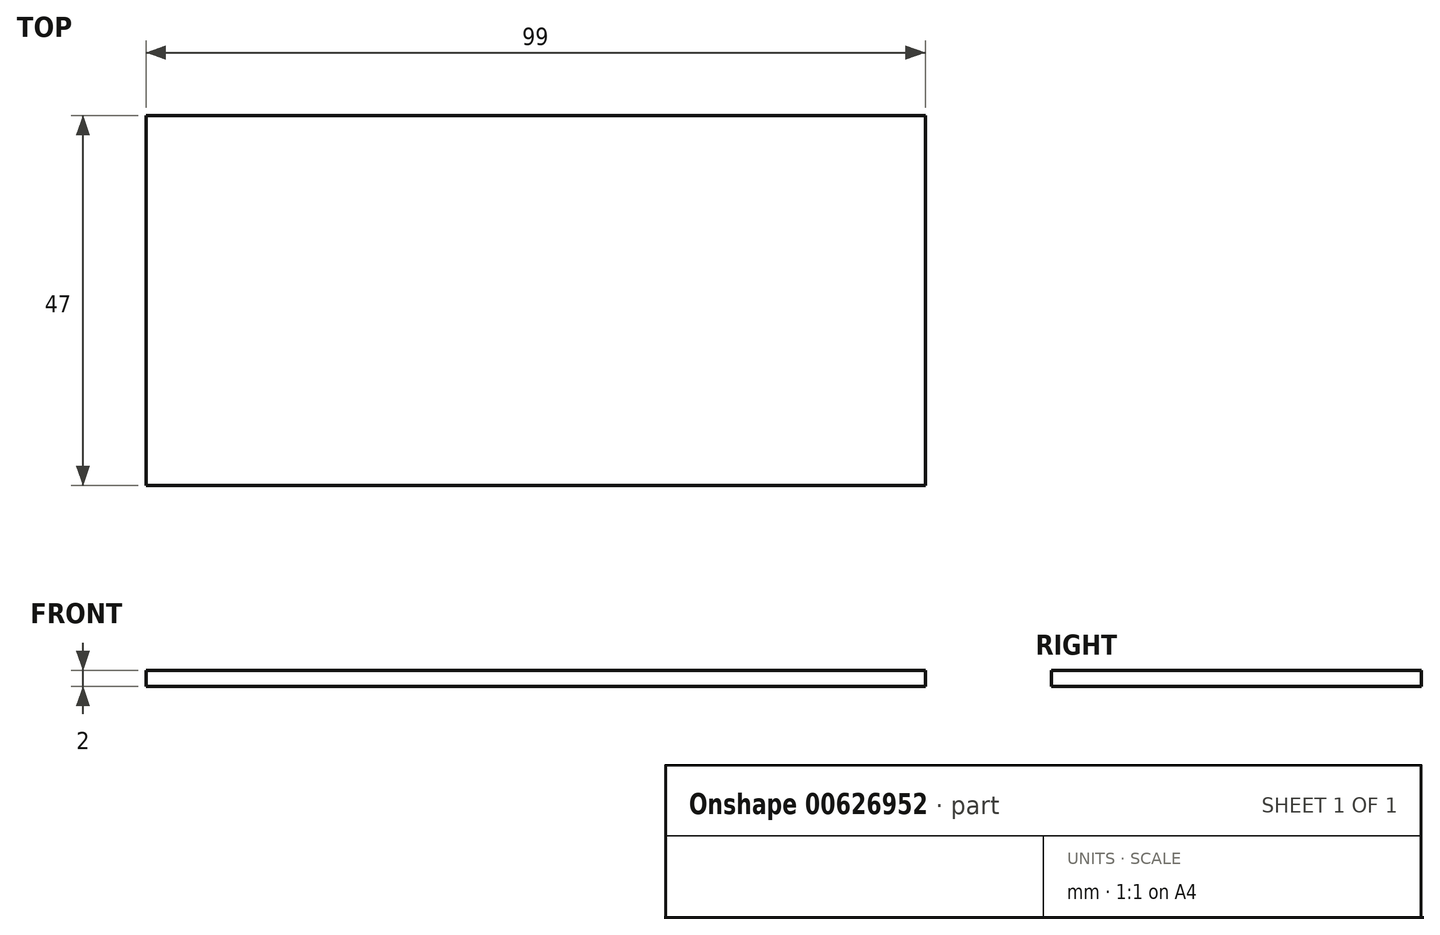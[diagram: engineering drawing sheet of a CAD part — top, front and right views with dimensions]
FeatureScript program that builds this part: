
annotation { "Feature Type Name" : "Feature", "Feature Type Description" : "" }
export const myFeature = defineFeature(function(context is Context, id is Id, definition is map)
    precondition{}
    {
        {
            var Q0;
            Q0=qCreatedBy(makeId("Top.planeOp"),FACE);
            var sketch = newSketch(context, id + "F0", { "sketchPlane" : qUnion([Q0])});
            skLineSegment(sketch, "E0.bottom", {"start": v(49.5, 23.5) * mm, "end": v(-49.5, 23.5) * mm});
            skLineSegment(sketch, "E0.top", {"start": v(49.5, -23.5) * mm, "end": v(-49.5, -23.5) * mm});
            skLineSegment(sketch, "E0.left", {"start": v(49.5, 23.5) * mm, "end": v(49.5, -23.5) * mm});
            skLineSegment(sketch, "E0.right", {"start": v(-49.5, 23.5) * mm, "end": v(-49.5, -23.5) * mm});
            skPoint(sketch, "E0.middle", {"position": v(0, 0) * mm});
            skLineSegment(sketch, "E1", {"start": v(28.5, -23.5) * mm, "end": v(28.5, 3.46) * mm, "construction": true});
            skSolve(sketch);
        }
        {
            var Q0;
            Q0=makeQuery(id+"F0.imprint","IMPRINT",FACE,{"disambiguationData":[TD([[makeQuery(id+"F0.imprint","IMPRINT",EDGE,{"derivedFrom":sQuery(id+"F0.wireOp",EDGE,"E0.bottom")}),1.0]])]});
            extrude(context, id + "F1", {"entities" : qUnion([Q0]), "depth" : 2 * mm, "offsetDistance" : 25 * mm});
        }
    });
